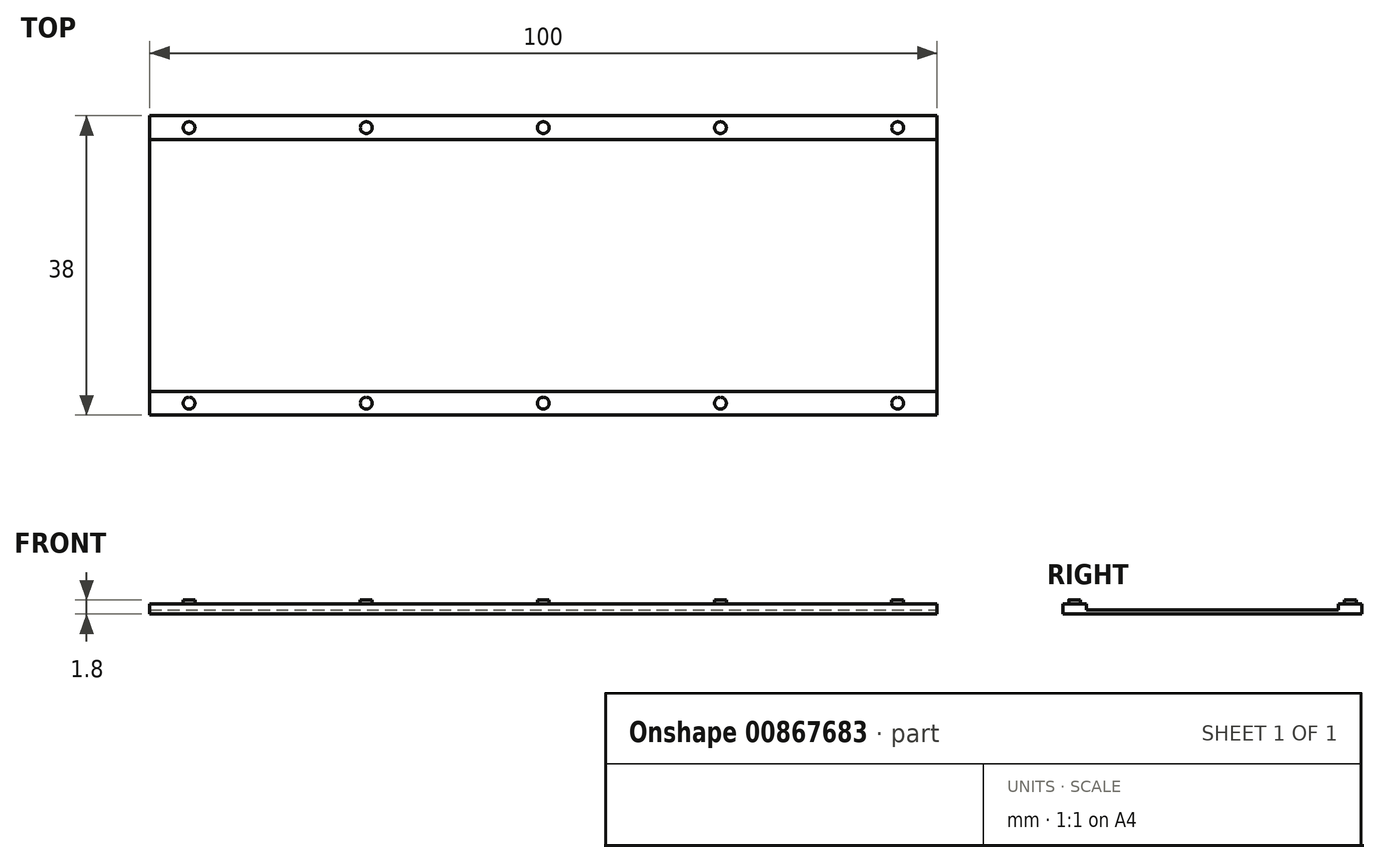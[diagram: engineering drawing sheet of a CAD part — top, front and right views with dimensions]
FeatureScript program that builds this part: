
annotation { "Feature Type Name" : "Feature", "Feature Type Description" : "" }
export const myFeature = defineFeature(function(context is Context, id is Id, definition is map)
    precondition{}
    {
        {
            var Q0;
            Q0=qCreatedBy(makeId("Top.planeOp"),FACE);
            var sketch = newSketch(context, id + "F0", { "sketchPlane" : qUnion([Q0])});
            skLineSegment(sketch, "E0.bottom", {"start": v(0, 19) * mm, "end": v(-100, 19) * mm});
            skLineSegment(sketch, "E0.top", {"start": v(0, -19) * mm, "end": v(-100, -19) * mm});
            skLineSegment(sketch, "E0.left", {"start": v(0, 19) * mm, "end": v(0, -19) * mm});
            skLineSegment(sketch, "E0.right", {"start": v(-100, 19) * mm, "end": v(-100, -19) * mm});
            skSolve(sketch);
        }
        {
            var Q0;
            Q0=makeQuery(id+"F0.imprint","IMPRINT",FACE,{"disambiguationData":[TD([[makeQuery(id+"F0.imprint","IMPRINT",EDGE,{"derivedFrom":sQuery(id+"F0.wireOp",EDGE,"E0.bottom")}),1.0]])]});
            var Q1;
            Q1=makeQuery(id+"F0.imprint","IMPRINT",FACE,{"disambiguationData":[TD([[makeQuery(id+"F0.imprint","IMPRINT",EDGE,{"derivedFrom":sQuery(id+"F0.wireOp",EDGE,"myi1CNZL-ncN6-KSQ3-Gm74-VcaZA40VpBcY.bottom")}),1.0]])]});
            extrude(context, id + "F1", {"entities" : qUnion([Q0, Q1]), "oppositeDirection" : true, "depth" : .5 * mm, "offsetDistance" : 25 * mm});
        }
        {
            var Q0;
            Q0=makeQuery(id+"F1.opExtrude","CAP_FACE",FACE,{"disambiguationData":[OSD([sQuery(id+"F0.wireOp",EDGE,"E0.bottom"),sQuery(id+"F0.wireOp",EDGE,"E0.top"),sQuery(id+"F0.wireOp",EDGE,"E0.left"),sQuery(id+"F0.wireOp",EDGE,"E0.right")])],"isStart":true});
            var sketch = newSketch(context, id + "F2", { "sketchPlane" : qUnion([Q0])});
            skLineSegment(sketch, "E1.bottom", {"start": v(-100, 19) * mm, "end": v(0, 19) * mm});
            skLineSegment(sketch, "E1.top", {"start": v(-100, 16) * mm, "end": v(0, 16) * mm});
            skLineSegment(sketch, "E1.left", {"start": v(-100, 19) * mm, "end": v(-100, 16) * mm});
            skLineSegment(sketch, "E1.right", {"start": v(0, 19) * mm, "end": v(0, 16) * mm});
            skLineSegment(sketch, "E2.bottom", {"start": v(-100, -19) * mm, "end": v(0, -19) * mm});
            skLineSegment(sketch, "E2.top", {"start": v(-100, -16) * mm, "end": v(0, -16) * mm});
            skLineSegment(sketch, "E2.left", {"start": v(-100, -19) * mm, "end": v(-100, -16) * mm});
            skLineSegment(sketch, "E2.right", {"start": v(0, -19) * mm, "end": v(0, -16) * mm});
            skSolve(sketch);
        }
        {
            var Q0;
            Q0=makeQuery(id+"F2.imprint","IMPRINT",FACE,{"disambiguationData":[TD([[makeQuery(id+"F2.imprint","IMPRINT",EDGE,{"derivedFrom":sQuery(id+"F2.wireOp",EDGE,"E1.bottom")}),1.0]])]});
            var Q1;
            Q1=makeQuery(id+"F2.imprint","IMPRINT",FACE,{"disambiguationData":[TD([[makeQuery(id+"F2.imprint","IMPRINT",EDGE,{"derivedFrom":sQuery(id+"F2.wireOp",EDGE,"E2.bottom")}),-1.0]])]});
            extrude(context, id + "F3", {"entities" : qUnion([Q0, Q1]), "operationType" : NewBodyOperationType.ADD, "depth" : .8 * mm, "offsetDistance" : 25 * mm});
        }
        {
            var Q0;
            Q0=makeQuery(id+"F3.opExtrude","CAP_FACE",FACE,{"disambiguationData":[OSD([sQuery(id+"F2.wireOp",EDGE,"E1.bottom"),sQuery(id+"F2.wireOp",EDGE,"E1.top"),sQuery(id+"F2.wireOp",EDGE,"E1.left"),sQuery(id+"F2.wireOp",EDGE,"E1.right")])],"isStart":false});
            var sketch = newSketch(context, id + "F4", { "sketchPlane" : qUnion([Q0])});
            skCircle(sketch, "E3", {"center": v(-95, 17.5) * mm, "radius": 0.75 * mm});
            skCircle(sketch, "E4.1.0.0", {"center": v(-72.5, 17.5) * mm, "radius": 0.75 * mm});
            skCircle(sketch, "E4.2.0.0", {"center": v(-50, 17.5) * mm, "radius": 0.75 * mm});
            skCircle(sketch, "E4.3.0.0", {"center": v(-27.5, 17.5) * mm, "radius": 0.75 * mm});
            skCircle(sketch, "E4.4.0.0", {"center": v(-5, 17.5) * mm, "radius": 0.75 * mm});
            skLineSegment(sketch, "E4.direction1", {"start": v(-95, 17.5) * mm, "end": v(-72.5, 17.5) * mm, "construction": true});
            skSolve(sketch);
        }
        {
            var Q0;
            Q0=makeQuery(id+"F4.imprint","IMPRINT",FACE,{"disambiguationData":[TD([[makeQuery(id+"F4.imprint","IMPRINT",EDGE,{"derivedFrom":sQuery(id+"F4.wireOp",EDGE,"E3")}),1.0]])]});
            var Q1;
            Q1=makeQuery(id+"F4.imprint","IMPRINT",FACE,{"disambiguationData":[TD([[makeQuery(id+"F4.imprint","IMPRINT",EDGE,{"derivedFrom":sQuery(id+"F4.wireOp",EDGE,"E4.1.0.0")}),1.0]])]});
            var Q2;
            Q2=makeQuery(id+"F4.imprint","IMPRINT",FACE,{"disambiguationData":[TD([[makeQuery(id+"F4.imprint","IMPRINT",EDGE,{"derivedFrom":sQuery(id+"F4.wireOp",EDGE,"E4.2.0.0")}),1.0]])]});
            var Q3;
            Q3=makeQuery(id+"F4.imprint","IMPRINT",FACE,{"disambiguationData":[TD([[makeQuery(id+"F4.imprint","IMPRINT",EDGE,{"derivedFrom":sQuery(id+"F4.wireOp",EDGE,"E4.3.0.0")}),1.0]])]});
            var Q4;
            Q4=makeQuery(id+"F4.imprint","IMPRINT",FACE,{"disambiguationData":[TD([[makeQuery(id+"F4.imprint","IMPRINT",EDGE,{"derivedFrom":sQuery(id+"F4.wireOp",EDGE,"E4.4.0.0")}),1.0]])]});
            extrude(context, id + "F5", {"entities" : qUnion([Q0, Q1, Q2, Q3, Q4]), "operationType" : NewBodyOperationType.ADD, "depth" : .5 * mm, "offsetDistance" : 25 * mm});
        }
        {
            var Q0;
            Q0=makeQuery(id+"F3.opExtrude","CAP_FACE",FACE,{"disambiguationData":[OSD([sQuery(id+"F2.wireOp",EDGE,"E2.bottom"),sQuery(id+"F2.wireOp",EDGE,"E2.top"),sQuery(id+"F2.wireOp",EDGE,"E2.left"),sQuery(id+"F2.wireOp",EDGE,"E2.right")])],"isStart":false});
            var sketch = newSketch(context, id + "F6", { "sketchPlane" : qUnion([Q0])});
            skCircle(sketch, "E5", {"center": v(-95, -17.5) * mm, "radius": 0.75 * mm});
            skCircle(sketch, "E6.1.0.0", {"center": v(-72.5, -17.5) * mm, "radius": 0.75 * mm});
            skCircle(sketch, "E6.2.0.0", {"center": v(-50, -17.5) * mm, "radius": 0.75 * mm});
            skCircle(sketch, "E6.3.0.0", {"center": v(-27.5, -17.5) * mm, "radius": 0.75 * mm});
            skCircle(sketch, "E6.4.0.0", {"center": v(-5, -17.5) * mm, "radius": 0.75 * mm});
            skLineSegment(sketch, "E6.direction1", {"start": v(-95, -17.5) * mm, "end": v(-72.5, -17.5) * mm, "construction": true});
            skSolve(sketch);
        }
        {
            var Q0;
            Q0=makeQuery(id+"F6.imprint","IMPRINT",FACE,{"disambiguationData":[TD([[makeQuery(id+"F6.imprint","IMPRINT",EDGE,{"derivedFrom":sQuery(id+"F6.wireOp",EDGE,"E5")}),1.0]])]});
            var Q1;
            Q1=makeQuery(id+"F6.imprint","IMPRINT",FACE,{"disambiguationData":[TD([[makeQuery(id+"F6.imprint","IMPRINT",EDGE,{"derivedFrom":sQuery(id+"F6.wireOp",EDGE,"E6.1.0.0")}),1.0]])]});
            var Q2;
            Q2=makeQuery(id+"F6.imprint","IMPRINT",FACE,{"disambiguationData":[TD([[makeQuery(id+"F6.imprint","IMPRINT",EDGE,{"derivedFrom":sQuery(id+"F6.wireOp",EDGE,"E6.2.0.0")}),1.0]])]});
            var Q3;
            Q3=makeQuery(id+"F6.imprint","IMPRINT",FACE,{"disambiguationData":[TD([[makeQuery(id+"F6.imprint","IMPRINT",EDGE,{"derivedFrom":sQuery(id+"F6.wireOp",EDGE,"E6.3.0.0")}),1.0]])]});
            var Q4;
            Q4=makeQuery(id+"F6.imprint","IMPRINT",FACE,{"disambiguationData":[TD([[makeQuery(id+"F6.imprint","IMPRINT",EDGE,{"derivedFrom":sQuery(id+"F6.wireOp",EDGE,"E6.4.0.0")}),1.0]])]});
            extrude(context, id + "F7", {"entities" : qUnion([Q0, Q1, Q2, Q3, Q4]), "operationType" : NewBodyOperationType.ADD, "depth" : .5 * mm, "offsetDistance" : 25 * mm});
        }
    });
